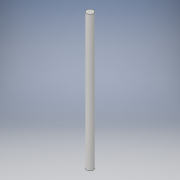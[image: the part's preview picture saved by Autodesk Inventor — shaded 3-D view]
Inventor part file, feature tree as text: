
AUTODESK INVENTOR PART (.ipt)
format: ipt  version: 2018 (Build 220112000, 112)  size: 88,576 bytes
history: native  units: in
note: dims shown in document units (in); Inventor stores cm internally (conversion verified against a paired STEP export)
features: extrude x1, sketch x1
ambient origin geometry x8: Origin, YZ Plane, XZ Plane, XY Plane, X Axis, Y Axis, Z Axis, Center Point
bodies: Solid1 (feature_tree)
feature tree (2):
  extrude  "Extrusion1"  Depth=15.0in TaperAngle=0.0deg
  sketch  "Sketch1"  dims[d0=0.75in d1=15.0in d2=0.0in]
